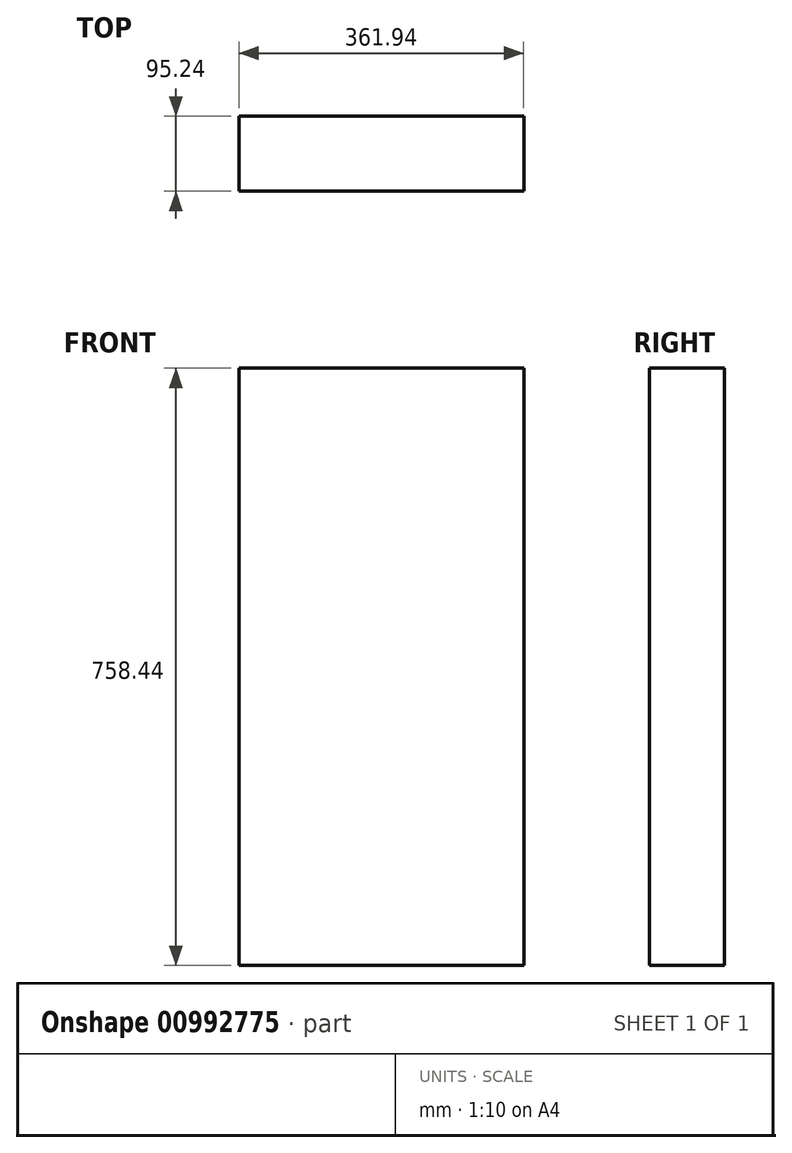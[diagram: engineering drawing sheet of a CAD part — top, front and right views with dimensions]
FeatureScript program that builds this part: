
annotation { "Feature Type Name" : "Feature", "Feature Type Description" : "" }
export const myFeature = defineFeature(function(context is Context, id is Id, definition is map)
    precondition{}
    {
        {
            var Q0;
            Q0=qCreatedBy(makeId("Top.planeOp"),FACE);
            var sketch = newSketch(context, id + "F0", { "sketchPlane" : qUnion([Q0])});
            skLineSegment(sketch, "E0.bottom", {"start": v(180.98, -47.62) * mm, "end": v(-180.97, -47.63) * mm});
            skLineSegment(sketch, "E0.top", {"start": v(180.97, 47.63) * mm, "end": v(-180.98, 47.63) * mm});
            skLineSegment(sketch, "E0.left", {"start": v(180.98, -47.62) * mm, "end": v(180.97, 47.63) * mm});
            skLineSegment(sketch, "E0.right", {"start": v(-180.98, -47.63) * mm, "end": v(-180.98, 47.63) * mm});
            skPoint(sketch, "E0.middle", {"position": v(0, 0) * mm});
            skSolve(sketch);
        }
        {
            var Q0;
            Q0 = qSketchRegion(id + "F0", true);
            extrude(context, id + "F1", {"entities" : qUnion([Q0]), "depth" : 758.44 * mm, "offsetDistance" : 25.4 * mm});
        }
    });
